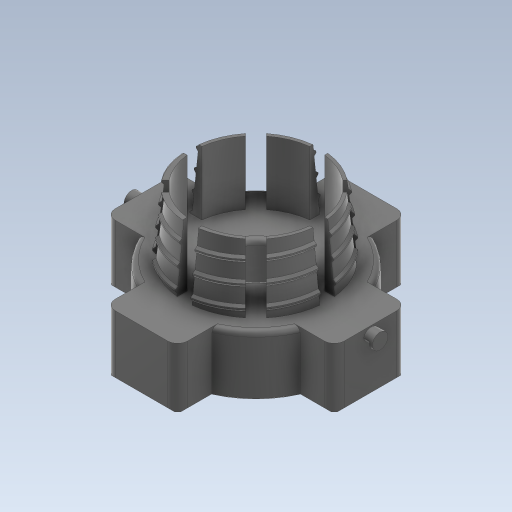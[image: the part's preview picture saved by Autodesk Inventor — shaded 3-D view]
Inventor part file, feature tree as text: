
AUTODESK INVENTOR PART (.ipt)
format: ipt  version: 2023 (Build 270158000, 158)  size: 2,229,760 bytes
history: native  units: mm
features: sketch x7, extrude x6, fillet x3, helix x2, draft x1, direct_edit x1, hole x1, pattern_circular x1, chamfer x1, projected_geometry x1, other x1
ambient origin geometry x8: Origin, YZ Plane, XZ Plane, XY Plane, X Axis, Y Axis, Z Axis, Center Point
bodies: Solid1 (feature_tree)
feature tree (25):
  extrude  "Extrusion1"  Depth=26.5mm
  draft  "FaceDraft1"
  sketch  "Sketch2"  dims[d34=0.0mm d35=0.0mm]
  helix  "Coil3"  [1 undecoded]
  helix  "Coil4"  [1 undecoded]
  direct_edit  "Direct Edit2"
  extrude  "Extrusion2"  Depth=12.0mm TaperAngle=0.0deg
  sketch  "Sketch4"  dims[d56=8.726646mm d62=4.0mm d63=13.0mm d64=10.0mm d65=1.047198mm]
  extrude  "Extrusion3"  Depth=10.0mm
  extrude  "Extrusion8"  TaperAngle=90.0deg  [1 undecoded]
  hole  "Hole1"  [1 undecoded]
  sketch  "Sketch9"  dims[d83=3.0mm d84=1.5mm d85=1.5mm d86=0.0mm d87=0.0mm d91=3.0mm d92=3.0mm d93=1.5mm d94=1.5mm d95=5.3mm d96=6.0mm d97=10.0mm d98=10.0mm d99=90.0deg d100=8.0mm d101=20.594885mm d108=35.6mm d110=3.15mm d113=1.575mm d114=7.45mm d115=2.35mm d117=3.6mm d118=0.0mm d119=1.2mm d120=0.0mm d121=20.0mm d122=360.0deg d126=1.0mm d129=0.3mm d130=2.0mm d131=45.0deg d133=14.65mm d134=14.65mm d137=23.15mm d138=46.3mm d139=46.3mm d142=1.0mm d143=2.0mm d109=0.5mm d111=0.5mm d112=0.872665mm]
  extrude  "Extrusion11"  Depth=2.0mm
  extrude  "Extrusion12"  Depth=2.0mm
  pattern_circular  "Circular Pattern1"  [2 undecoded]
  fillet  "Fillet4"  Radius=3.0mm
  chamfer  "Chamfer2"  Distance=3.0mm
  fillet  "Fillet7"  Radius=1.5mm
  fillet  "Fillet8"  Radius=1.5mm
  sketch  "Sketch1"  dims[d0=25.0mm d1=26.5mm d2=12.875mm d3=0.0mm d4=1.047198mm]
  sketch  "Sketch3"  dims[d36=7.325mm d37=7.0mm d38=7.325mm d39=0.0mm d40=7.0mm d41=28.73603mm d42=12.0mm d43=0.0mm]
  sketch  "Sketch5"  dims[d66=90.0deg d67=90.0deg d68=0.0mm d69=0.0mm d70=4.0mm d71=3.0mm d72=10.0mm d73=-1.047198mm d74=90.0deg d75=90.0deg d76=0.0mm d77=0.0mm]
  sketch  "Sketch7"  dims[d79=-0.127mm d82=3.0mm]
  projected_geometry  "Projected Loop1"
  other  "Size2"
note: 6 required parameter values undecoded (feature->parameter linkage not recoverable at this tier; creation-order binding heuristic only, values carry confidence <= 0.55)
